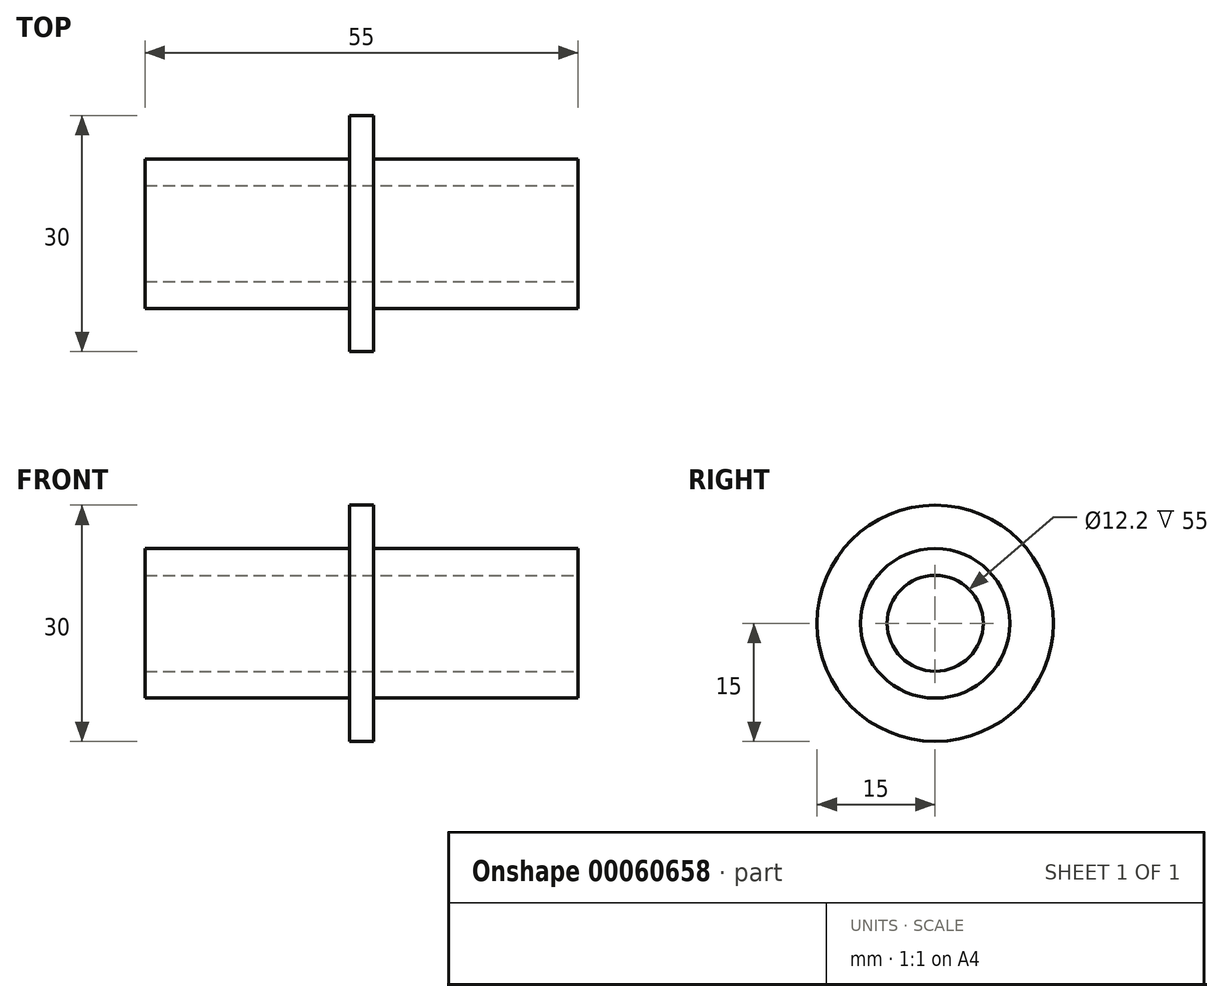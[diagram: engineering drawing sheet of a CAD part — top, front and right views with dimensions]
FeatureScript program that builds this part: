
annotation { "Feature Type Name" : "Feature", "Feature Type Description" : "" }
export const myFeature = defineFeature(function(context is Context, id is Id, definition is map)
    precondition{}
    {
        {
            var Q0;
            Q0=qCreatedBy(makeId("Right.planeOp"),FACE);
            var sketch = newSketch(context, id + "F0", { "sketchPlane" : qUnion([Q0])});
            skCircle(sketch, "E0", {"center": v(0, 0) * mm, "radius": 9.5 * mm});
            skCircle(sketch, "E1", {"center": v(0, 0) * mm, "radius": 6.1 * mm});
            skCircle(sketch, "E2", {"center": v(0, 0) * mm, "radius": 15 * mm});
            skSolve(sketch);
        }
        {
            var Q0;
            Q0=makeQuery(id+"F0.imprint","IMPRINT",FACE,{"disambiguationData":[TD([[makeQuery(id+"F0.imprint","IMPRINT",EDGE,{"derivedFrom":sQuery(id+"F0.wireOp",EDGE,"E0")}),1.0]])]});
            extrude(context, id + "F1", {"entities" : qUnion([Q0]), "oppositeDirection" : true, "depth" : 58 * mm, "hasSecondDirection" : true, "secondDirectionOppositeDirection" : true, "secondDirectionDepth" : 3 * mm});
        }
        {
            var Q0;
            Q0=makeQuery(id+"F0.imprint","IMPRINT",FACE,{"disambiguationData":[TD([[makeQuery(id+"F0.imprint","IMPRINT",EDGE,{"derivedFrom":sQuery(id+"F0.wireOp",EDGE,"E0")}),-1.0]])]});
            var Q1;
            Q1=sQuery(id+"F0.wireOp",EDGE,"E0");
            extrude(context, id + "F2", {"entities" : qUnion([Q0]), "operationType" : NewBodyOperationType.ADD, "surfaceEntities" : qUnion([Q1]), "oppositeDirection" : true, "depth" : 32 * mm, "hasSecondDirection" : true, "secondDirectionOppositeDirection" : true, "secondDirectionDepth" : 29 * mm});
        }
    });
